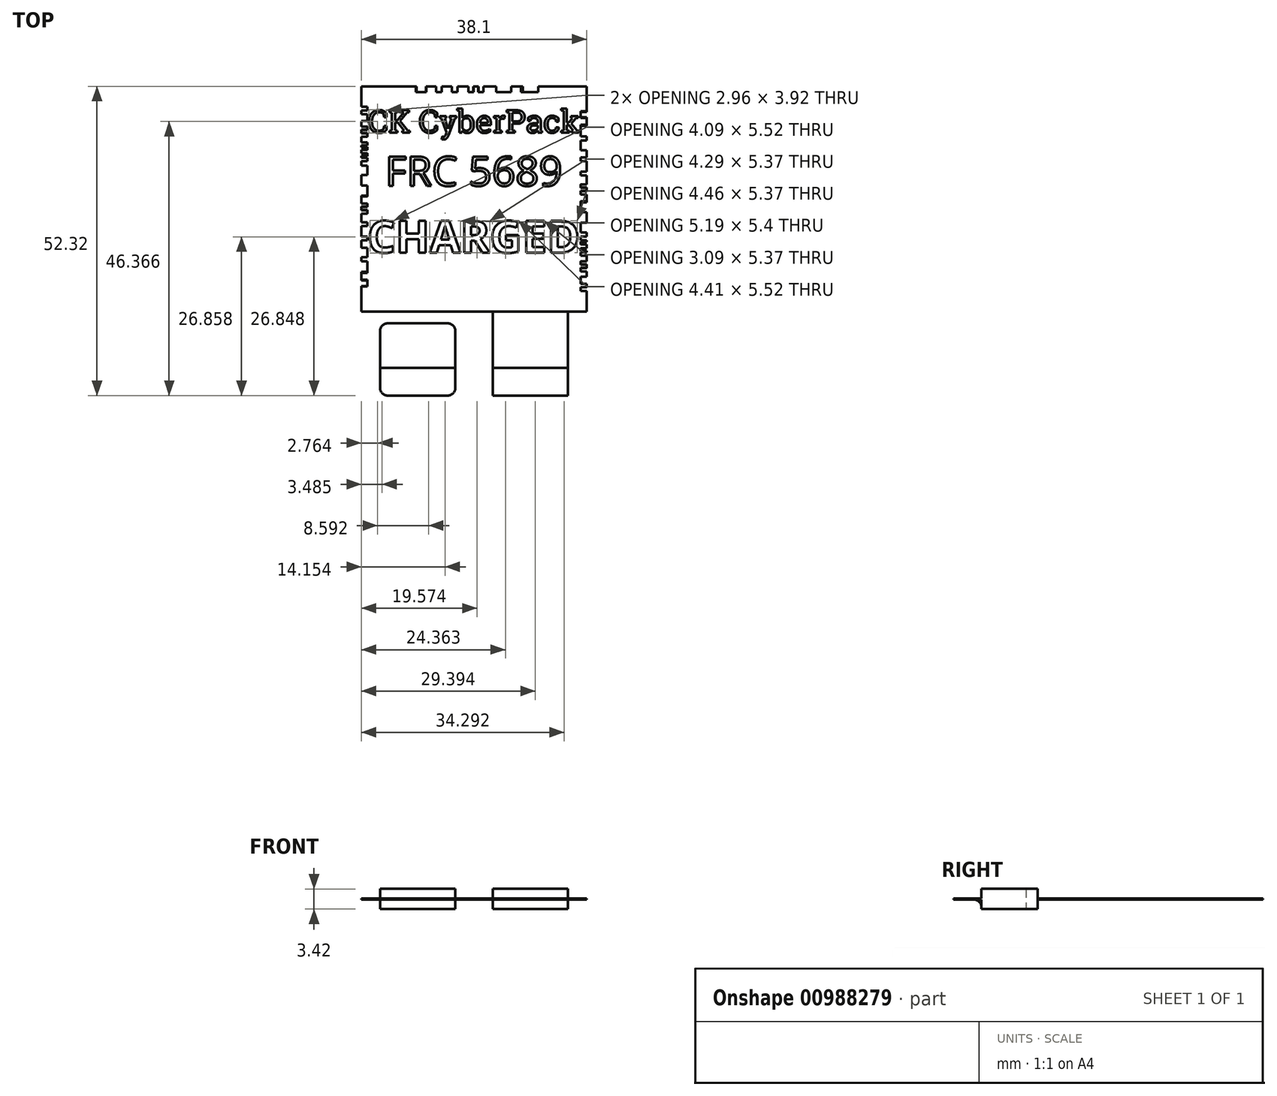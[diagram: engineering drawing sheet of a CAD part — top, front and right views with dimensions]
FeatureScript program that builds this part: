
annotation { "Feature Type Name" : "Feature", "Feature Type Description" : "" }
export const myFeature = defineFeature(function(context is Context, id is Id, definition is map)
    precondition{}
    {
        {
            var Q0;
            Q0=qCreatedBy(makeId("Top.planeOp"),FACE);
            var sketch = newSketch(context, id + "F0", { "sketchPlane" : qUnion([Q0])});
            skLineSegment(sketch, "E0.bottom", {"start": v(-19.05, 19.05) * mm, "end": v(19.05, 19.05) * mm});
            skLineSegment(sketch, "E0.top", {"start": v(-19.05, -19.05) * mm, "end": v(19.05, -19.05) * mm});
            skLineSegment(sketch, "E0.left", {"start": v(-19.05, 19.05) * mm, "end": v(-19.05, -19.05) * mm});
            skLineSegment(sketch, "E0.right", {"start": v(19.05, 19.05) * mm, "end": v(19.05, -19.05) * mm});
            skPoint(sketch, "E0.middle", {"position": v(0, 0) * mm});
            skLineSegment(sketch, "E1.bottom", {"start": v(-15.88, -19.05) * mm, "end": v(-3.18, -19.05) * mm});
            skLineSegment(sketch, "E1.top", {"start": v(-15.88, -28.58) * mm, "end": v(-3.18, -28.58) * mm});
            skLineSegment(sketch, "E1.left", {"start": v(-15.88, -19.05) * mm, "end": v(-15.88, -28.58) * mm});
            skLineSegment(sketch, "E1.right", {"start": v(-3.18, -19.05) * mm, "end": v(-3.18, -28.58) * mm});
            skLineSegment(sketch, "E2.bottom", {"start": v(-15.88, -33.27) * mm, "end": v(-3.18, -33.27) * mm});
            skLineSegment(sketch, "E2.left", {"start": v(-15.88, -28.58) * mm, "end": v(-15.88, -33.27) * mm});
            skLineSegment(sketch, "E2.right", {"start": v(-3.18, -28.58) * mm, "end": v(-3.18, -33.27) * mm});
            skLineSegment(sketch, "E3", {"start": v(0, 36.29) * mm, "end": v(0, -56.4) * mm, "construction": true});
            skLineSegment(sketch, "E4.MirrorCS", {"start": v(15.88, -28.58) * mm, "end": v(3.18, -28.58) * mm});
            skLineSegment(sketch, "E5.MirrorCS", {"start": v(15.88, -28.58) * mm, "end": v(15.88, -33.27) * mm});
            skLineSegment(sketch, "E6.MirrorCS", {"start": v(3.18, -28.58) * mm, "end": v(3.18, -33.27) * mm});
            skLineSegment(sketch, "E7.MirrorCS", {"start": v(15.88, -33.27) * mm, "end": v(3.18, -33.27) * mm});
            skLineSegment(sketch, "E8.MirrorCS", {"start": v(15.88, -19.05) * mm, "end": v(15.88, -28.58) * mm});
            skLineSegment(sketch, "E9.MirrorCS", {"start": v(3.18, -19.05) * mm, "end": v(3.18, -28.58) * mm});
            skLineSegment(sketch, "E10", {"start": v(-15.88, -21.06) * mm, "end": v(-3.18, -21.06) * mm});
            skLineSegment(sketch, "E11.MirrorCS", {"start": v(15.88, -21.06) * mm, "end": v(3.18, -21.06) * mm});
            skSolve(sketch);
        }
        {
            assignVariable(context, id + "F1", {"name" : "Thickness_Main", "anyValue" : .20});
        }
        {
            var Q0;
            Q0=makeQuery(id+"F0.imprint","IMPRINT",FACE,{"disambiguationData":[TD([[makeQuery(id+"F0.imprint","IMPRINT",EDGE,{"derivedFrom":sQuery(id+"F0.wireOp",EDGE,"E0.bottom")}),-1.0]])]});
            extrude(context, id + "F2", {"entities" : qUnion([Q0]), "endBound" : BoundingType.SYMMETRIC, "depth" : (getVariable(context, 'Thickness_Main')) * mm});
        }
        {
            var Q0;
            {var subQ0=sQuery(id+"F0.wireOp",EDGE,"E1.top");Q0=makeQuery(id+"F0.imprint","IMPRINT",FACE,{"disambiguationData":[TD([[makeQuery(id+"F0.imprint","IMPRINT",EDGE,{"derivedFrom":subQ0}),1.0]])]});}
            var Q1;
            {var subQ0=sQuery(id+"F0.wireOp",EDGE,"E4.MirrorCS");Q1=makeQuery(id+"F0.imprint","IMPRINT",FACE,{"disambiguationData":[TD([[makeQuery(id+"F0.imprint","IMPRINT",EDGE,{"derivedFrom":subQ0}),-1.0]])]});}
            var Q2;
            {var subQ0=sQuery(id+"F0.wireOp",EDGE,"E1.bottom");Q2=makeQuery(id+"F0.imprint","IMPRINT",FACE,{"disambiguationData":[TD([[makeQuery(id+"F0.imprint","IMPRINT",EDGE,{"derivedFrom":subQ0}),-1.0]])]});}
            var Q3;
            {var subQ5=sQuery(id+"F0.wireOp",EDGE,"E11.MirrorCS");Q3=makeQuery(id+"F0.imprint","IMPRINT",FACE,{"disambiguationData":[TD([[makeQuery(id+"F0.imprint","IMPRINT",EDGE,{"derivedFrom":subQ5}),-1.0]])]});}
            extrude(context, id + "F3", {"entities" : qUnion([Q0, Q1, Q2, Q3]), "operationType" : NewBodyOperationType.ADD, "endBound" : BoundingType.SYMMETRIC, "depth" : 3.43 * mm});
        }
        {
            var Q0;
            Q0=makeQuery(id+"F0.imprint","IMPRINT",FACE,{"disambiguationData":[TD([[makeQuery(id+"F0.imprint","IMPRINT",EDGE,{"derivedFrom":sQuery(id+"F0.wireOp",EDGE,"E2.bottom")}),1.0]])]});
            var Q1;
            Q1=makeQuery(id+"F0.imprint","IMPRINT",FACE,{"disambiguationData":[TD([[makeQuery(id+"F0.imprint","IMPRINT",EDGE,{"derivedFrom":sQuery(id+"F0.wireOp",EDGE,"E5.MirrorCS")}),-1.0]])]});
            var Q2;
            Q2=makeQuery(id+"F2.opExtrude","CAP_FACE",FACE,{"disambiguationData":[OSD([sQuery(id+"F0.wireOp",EDGE,"E0.bottom"),sQuery(id+"F0.wireOp",EDGE,"E0.top"),sQuery(id+"F0.wireOp",EDGE,"E0.left"),sQuery(id+"F0.wireOp",EDGE,"E0.right"),sQuery(id+"F0.wireOp",EDGE,"E1.bottom"),sQuery(id+"F0.wireOp",EDGE,"7qUCwU1O-SrLC-5cXe-5013-sIu5dsXMdAK1")])],"isStart":false});
            var Q3;
            Q3=makeQuery(id+"F2.opExtrude","CAP_FACE",FACE,{"disambiguationData":[OSD([sQuery(id+"F0.wireOp",EDGE,"E0.bottom"),sQuery(id+"F0.wireOp",EDGE,"E0.top"),sQuery(id+"F0.wireOp",EDGE,"E0.left"),sQuery(id+"F0.wireOp",EDGE,"E0.right"),sQuery(id+"F0.wireOp",EDGE,"E1.bottom"),sQuery(id+"F0.wireOp",EDGE,"7qUCwU1O-SrLC-5cXe-5013-sIu5dsXMdAK1")])],"isStart":true});
            extrude(context, id + "F4", {"entities" : qUnion([Q0, Q1]), "operationType" : NewBodyOperationType.ADD, "endBound" : BoundingType.UP_TO_SURFACE, "endBoundEntityFace" : qUnion([Q2]), "depth" : (getVariable(context, 'Thickness_Main')) * mm, "hasSecondDirection" : true, "secondDirectionBound" : SecondDirectionBoundingType.UP_TO_SURFACE, "secondDirectionOppositeDirection" : true, "secondDirectionBoundEntityFace" : qUnion([Q3]), "secondDirectionDepth" : 25.4 * mm});
        }
        {
            var Q0;
            Q0=makeQuery(id+"F2.opExtrude","SWEPT_EDGE",EDGE,{"disambiguationData":[OSD([sQuery(id+"F0.wireOp",EDGE,"E0.top"),sQuery(id+"F0.wireOp",EDGE,"E1.bottom"),sQuery(id+"F0.wireOp",EDGE,"E1.right")])]});
            var Q1;
            Q1=makeQuery(id+"F2.opExtrude","SWEPT_EDGE",EDGE,{"disambiguationData":[OSD([sQuery(id+"F0.wireOp",EDGE,"E0.top"),sQuery(id+"F0.wireOp",EDGE,"E9.MirrorCS")])]});
            var Q2;
            Q2=makeQuery(id+"F2.opExtrude","SWEPT_EDGE",EDGE,{"disambiguationData":[OSD([sQuery(id+"F0.wireOp",EDGE,"E0.top"),sQuery(id+"F0.wireOp",EDGE,"E8.MirrorCS")])]});
            var Q3;
            Q3=makeQuery(id+"F2.opExtrude","SWEPT_EDGE",EDGE,{"disambiguationData":[OSD([sQuery(id+"F0.wireOp",EDGE,"E0.top"),sQuery(id+"F0.wireOp",EDGE,"E1.bottom"),sQuery(id+"F0.wireOp",EDGE,"E1.left")])]});
            var Q4;
            Q4=makeQuery(id+"F4.opExtrude","SWEPT_EDGE",EDGE,{"disambiguationData":[OSD([sQuery(id+"F0.wireOp",EDGE,"E5.MirrorCS"),sQuery(id+"F0.wireOp",EDGE,"E7.MirrorCS")])]});
            var Q5;
            Q5=makeQuery(id+"F4.opExtrude","SWEPT_EDGE",EDGE,{"disambiguationData":[OSD([sQuery(id+"F0.wireOp",EDGE,"E2.bottom"),sQuery(id+"F0.wireOp",EDGE,"E2.right")])]});
            var Q6;
            Q6=makeQuery(id+"F4.opExtrude","SWEPT_EDGE",EDGE,{"disambiguationData":[OSD([sQuery(id+"F0.wireOp",EDGE,"E6.MirrorCS"),sQuery(id+"F0.wireOp",EDGE,"E7.MirrorCS")])]});
            var Q7;
            Q7=makeQuery(id+"F4.opExtrude","SWEPT_EDGE",EDGE,{"disambiguationData":[OSD([sQuery(id+"F0.wireOp",EDGE,"E2.bottom"),sQuery(id+"F0.wireOp",EDGE,"E2.left")])]});
            var Q8;
            Q8=makeQuery(id+"F3.opExtrude","SWEPT_EDGE",EDGE,{"disambiguationData":[OSD([sQuery(id+"F0.wireOp",EDGE,"E0.top"),sQuery(id+"F0.wireOp",EDGE,"E1.bottom"),sQuery(id+"F0.wireOp",EDGE,"E1.right")])]});
            var Q9;
            Q9=makeQuery(id+"F3.opExtrude","SWEPT_EDGE",EDGE,{"disambiguationData":[OSD([sQuery(id+"F0.wireOp",EDGE,"E0.top"),sQuery(id+"F0.wireOp",EDGE,"E8.MirrorCS")])]});
            var Q10;
            Q10=makeQuery(id+"F3.opExtrude","SWEPT_EDGE",EDGE,{"disambiguationData":[OSD([sQuery(id+"F0.wireOp",EDGE,"E0.top"),sQuery(id+"F0.wireOp",EDGE,"E9.MirrorCS")])]});
            var Q11;
            Q11=makeQuery(id+"F3.opExtrude","SWEPT_EDGE",EDGE,{"disambiguationData":[OSD([sQuery(id+"F0.wireOp",EDGE,"E0.top"),sQuery(id+"F0.wireOp",EDGE,"E1.bottom"),sQuery(id+"F0.wireOp",EDGE,"E1.left")])]});
            var Q12;
            Q12=makeQuery(id+"F2.opExtrude","SWEPT_EDGE",EDGE,{"disambiguationData":[OSD([sQuery(id+"F0.wireOp",EDGE,"E0.bottom"),sQuery(id+"F0.wireOp",EDGE,"E0.right")])]});
            var Q13;
            Q13=makeQuery(id+"F2.opExtrude","SWEPT_EDGE",EDGE,{"disambiguationData":[OSD([sQuery(id+"F0.wireOp",EDGE,"E0.bottom"),sQuery(id+"F0.wireOp",EDGE,"E0.left")])]});
            var Q14;
            Q14=makeQuery(id+"F4.opExtrude","CAP_EDGE",EDGE,{"disambiguationData":[OSD([sQuery(id+"F0.wireOp",EDGE,"E1.top")])],"isStart":false});
            var Q15;
            Q15=makeQuery(id+"F4.opExtrude","CAP_EDGE",EDGE,{"disambiguationData":[OSD([sQuery(id+"F0.wireOp",EDGE,"E4.MirrorCS")])],"isStart":false});
            var Q16;
            Q16=makeQuery(id+"F4.opExtrude","CAP_EDGE",EDGE,{"disambiguationData":[OSD([sQuery(id+"F0.wireOp",EDGE,"E1.top")])],"isStart":true});
            var Q17;
            Q17=makeQuery(id+"F4.opExtrude","CAP_EDGE",EDGE,{"disambiguationData":[OSD([sQuery(id+"F0.wireOp",EDGE,"E4.MirrorCS")])],"isStart":true});
            fillet(context, id + "F5", {"entities" : qUnion([Q0, Q1, Q2, Q3, Q4, Q5, Q6, Q7, Q8, Q9, Q10, Q11, Q12, Q13, Q14, Q15, Q16, Q17]), "radius" : 1.27 * mm, "tangentPropagation" : true, "allowEdgeOverflow" : false});
        }
        {
            var Q0;
            Q0=makeQuery(id+"F2.opExtrude","CAP_FACE",FACE,{"disambiguationData":[OSD([sQuery(id+"F0.wireOp",EDGE,"E0.bottom"),sQuery(id+"F0.wireOp",EDGE,"E0.top"),sQuery(id+"F0.wireOp",EDGE,"E0.left"),sQuery(id+"F0.wireOp",EDGE,"E0.right"),sQuery(id+"F0.wireOp",EDGE,"E1.bottom")])],"isStart":false});
            var sketch = newSketch(context, id + "F6", { "sketchPlane" : qUnion([Q0])});
            skText(sketch, "E12", { "text": "CK CyberPack", "fontName": "RobotoSlab-Regular.ttf"});
            skText(sketch, "E13", { "text": "CHARGED", "fontName": "NotoSans-Bold.ttf"});
            skText(sketch, "E14", { "text": "FRC 5689", "fontName": "OpenSans-Regular.ttf"});
            const initialGuessF6  = {"E12": [-0.01795, 0.01119, 1, 0, 0.00386], "E13": [-0.01805, -0.00911, 1, 0, 0.00542], "E14": [-0.015, 0.0022, 1, 0, 0.005]};
            skSetInitialGuess(sketch, initialGuessF6);
            skSolve(sketch);
        }
        {
            var Q0;
            Q0 = qSketchRegion(id + "F6", true);
            extrude(context, id + "F7", {"entities" : qUnion([Q0]), "operationType" : NewBodyOperationType.REMOVE, "oppositeDirection" : true, "depth" : 1.5 * mm, "offsetDistance" : 25 * mm});
        }
        {
            var Q0;
            Q0=makeQuery(id+"F2.opExtrude","SWEPT_FACE",FACE,{"disambiguationData":[OSD([sQuery(id+"F0.wireOp",EDGE,"E0.bottom")])]});
            var sketch = newSketch(context, id + "F8", { "sketchPlane" : qUnion([Q0])});
            skText(sketch, "E15", { "text": "READY", "fontName": "RobotoSlab-Bold.ttf"});
            const initialGuessF8  = {"E15": [-0.01155, -0.0024, 1, 0, 0.0048]};
            skSetInitialGuess(sketch, initialGuessF8);
            skSolve(sketch);
        }
        {
            var Q0;
            Q0 = qSketchRegion(id + "F8", true);
            extrude(context, id + "F9", {"entities" : qUnion([Q0]), "operationType" : NewBodyOperationType.REMOVE, "oppositeDirection" : true, "depth" : 1 * mm, "offsetDistance" : 25 * mm});
        }
        {
            var Q0;
            Q0=makeQuery(id+"F2.opExtrude","SWEPT_FACE",FACE,{"disambiguationData":[OSD([sQuery(id+"F0.wireOp",EDGE,"E0.left")])]});
            var sketch = newSketch(context, id + "F10", { "sketchPlane" : qUnion([Q0])});
            skText(sketch, "E16", { "text": "GAME BATTERY", "fontName": "OpenSans-Bold.ttf"});
            skLineSegment(sketch, "E17.bottom", {"start": v(-17.78, 2.54) * mm, "end": v(17.78, 2.54) * mm, "construction": true});
            skLineSegment(sketch, "E17.top", {"start": v(-17.78, -2.54) * mm, "end": v(17.78, -2.54) * mm, "construction": true});
            skLineSegment(sketch, "E17.left", {"start": v(-17.78, 2.54) * mm, "end": v(-17.78, -2.54) * mm, "construction": true});
            skLineSegment(sketch, "E17.right", {"start": v(17.78, 2.54) * mm, "end": v(17.78, -2.54) * mm, "construction": true});
            const initialGuessF10  = {"E16": [-0.01585, -0.00154, 1, 0, 0.003]};
            skSetInitialGuess(sketch, initialGuessF10);
            skSolve(sketch);
        }
        {
            var Q0;
            Q0 = qSketchRegion(id + "F10", true);
            extrude(context, id + "F11", {"entities" : qUnion([Q0]), "operationType" : NewBodyOperationType.REMOVE, "oppositeDirection" : true, "depth" : 1 * mm, "offsetDistance" : 25 * mm});
        }
        {
            var Q0;
            Q0=makeQuery(id+"F2.opExtrude","SWEPT_FACE",FACE,{"disambiguationData":[OSD([sQuery(id+"F0.wireOp",EDGE,"E0.right")])]});
            var sketch = newSketch(context, id + "F12", { "sketchPlane" : qUnion([Q0])});
            skText(sketch, "E18", { "text": "GAME BATTERY", "fontName": "OpenSans-Bold.ttf"});
            const initialGuessF12  = {"E18": [-0.01585, -0.00154, 1, 0, 0.003]};
            skSetInitialGuess(sketch, initialGuessF12);
            skSolve(sketch);
        }
        {
            var Q0;
            Q0 = qSketchRegion(id + "F12", true);
            extrude(context, id + "F13", {"entities" : qUnion([Q0]), "operationType" : NewBodyOperationType.REMOVE, "oppositeDirection" : true, "depth" : 1 * mm, "offsetDistance" : 25 * mm});
        }
    });
